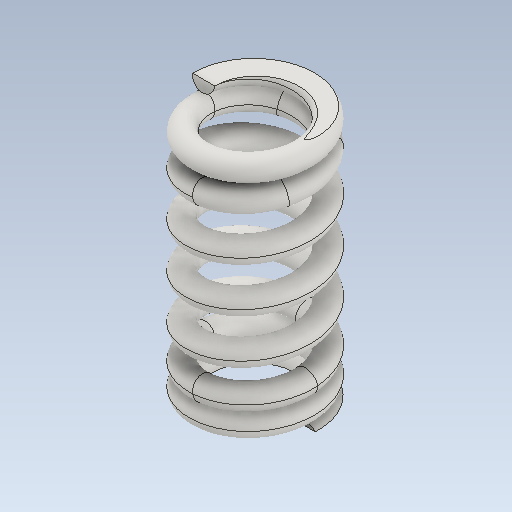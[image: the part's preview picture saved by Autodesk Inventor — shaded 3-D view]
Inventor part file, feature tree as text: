
AUTODESK INVENTOR PART (.ipt)
format: ipt  version: 2021 (Build 250183000, 183)  size: 1,066,496 bytes
history: native  units: mm
features: other x67, extrude x8, helix x5, sketch x3, sweep x2, plane x1
ambient origin geometry x8: Origin, YZ Plane, XZ Plane, XY Plane, X Axis, Y Axis, Z Axis, Center Point
bodies: Solid1 (feature_tree)
feature tree (86):
  other  "Main Coil Path(Right)"
  other  "Section Work Plane(Right)"
  other  "Start Work Plane(Right)"
  other  "End Work Plane(Right)"
  other  "End Cut Work Plane(Right)"
  other  "Start Cut Work Plane(Right)"
  other  "Plain Ends Cut Work Plane 1(Right)"
  other  "Plain Ends Cut Work Plane 2(Right)"
  sweep  "Main Coil Feature(R)"
  other  "Start Transition Coil 1(Right)"
  helix  "Coil  Start Transition 2(R)"  [1 undecoded]
  helix  "Coil  Start Transition 3(R)"  [1 undecoded]
  helix  "Coil  Start Transition 4(R)"  [1 undecoded]
  other  "Start Ends Coil(Right)"
  extrude  "Start Cut Feature(Right)"  Depth=10.0mm
  other  "End Transition Coil 1(Right)"
  other  "End Transition Coil 2(Right)"
  other  "End Transition Coil 3(Right)"
  other  "End Transition Coil 4(Right)"
  other  "End Coil(Right)"
  extrude  "End Cut Feature(Right)"  Depth=10.0mm
  extrude  "Plain Ends Cut Feature 1(Right)"  Depth=10.0mm
  extrude  "Plain Ends Cut  2(R)"  Depth=10.0mm TaperAngle=0.0deg
  other  "Main Coil Path(Left)"
  other  "Section Work Plane(Left)"
  other  "Start Work Plane(Left)"
  other  "End Work Plane(Left)"
  other  "End Cut Work Plane(Left)"
  other  "Start Cut Work Plane(Left)"
  other  "Plain Ends Cut Work Plane 1(Left)"
  other  "Plain Ends Cut Work Plane 2(Left)"
  sweep  "Main Coil Feature(L)"
  other  "Start Transition Coil 1(Left)"
  other  "Start Transition Coil 2(Left)"
  other  "Start Transition Coil 3(Left)"
  other  "Start Transition Coil 4(Left)"
  other  "Start Ends Coil(Left)"
  extrude  "Start Cut Feature(Left)"  Depth=10.0mm TaperAngle=0.0deg
  other  "End Transition Coil 1(Left)"
  other  "End Transition Coil 2(Left)"
  other  "End Transition Coil 3(Left)"
  other  "End Transition Coil 4(Left)"
  other  "End Coil(Left)"
  extrude  "End Cut Feature(Left)"  Depth=10.0mm
  extrude  "Cut Plain Ends Cut 1(L)"  TaperAngle=0.0deg  [1 undecoded]
  extrude  "Cut Plain Ends Cut 2(L)"  TaperAngle=0.0deg  [1 undecoded]
  other  "iMate Based Work Plane"
  other  "Preview Center Point"
  other  "Preview X Axis"
  other  "Path Section Sketch(Right)"
  other  "Srf1"
  helix  "Coil Section Sketch(Right)"  [1 undecoded]
  other  "Start Transition Coil Sketch 1(Right)"
  sketch  "Sketch  Start Transition 2(R)"  dims[d0=1.775mm d2=14.264373mm d3=10.0mm d4=32.5mm]
  sketch  "Sketch  Start Transition 3(R)"  dims[d5=0.0mm d6=90.0deg d7=90.0deg d8=0.0mm d9=0.0mm d12=14.440296mm d13=-18.678777mm d14=7.1mm]
  sketch  "Sketch  Start Transition 4(R)"  dims[d15=0.0mm d16=12.47328mm d17=10.0mm d18=2.5mm d19=0.0mm d20=90.0deg d21=90.0deg d22=0.0mm d23=0.0mm d24=10.682187mm d25=10.0mm d26=2.5mm d27=0.0mm d28=90.0deg d29=90.0deg d30=0.0mm d31=0.0mm d32=8.891093mm d33=10.0mm d34=2.5mm d35=0.0mm d36=90.0deg d37=90.0deg d38=0.0mm d39=0.0mm d40=7.1mm d41=10.0mm d42=2.5mm d43=0.0mm d44=90.0deg d45=90.0deg d46=0.0mm d47=0.0mm d48=12.47328mm d49=10.0mm d50=1.875mm d51=0.0mm d52=90.0deg d53=90.0deg d54=0.0mm d55=0.0mm d56=10.682187mm d57=10.0mm d58=1.875mm d59=0.0mm d60=90.0deg d61=90.0deg d62=0.0mm d63=0.0mm d64=8.891093mm d65=10.0mm d66=1.875mm d67=0.0mm d68=90.0deg d69=90.0deg d70=0.0mm d71=0.0mm d72=7.1mm d73=10.0mm d74=1.875mm d75=0.0mm d76=90.0deg d77=90.0deg d78=0.0mm d79=0.0mm d81=10.0mm d82=15.0mm d83=0.0mm d84=90.0deg d85=90.0deg d86=0.0mm d87=0.0mm d88=7.167284mm d89=10.0mm d90=10.0mm d91=0.0mm d92=90.0deg d93=90.0deg d94=0.0mm d95=0.0mm d96=40.003mm d97=7.167284mm d98=0.0mm d99=40.003mm d100=7.167284mm d101=0.0mm d102=0.0mm d103=0.0mm d104=0.0mm d105=0.0mm d106=0.0mm d108=0.0mm d112=0.0mm d113=0.0mm d114=0.0mm d121=1.858789mm d131=0.0mm d132=0.0mm d133=0.0mm d134=0.0mm d135=1.775mm d137=14.264373mm d138=10.0mm d139=32.5mm d140=0.0mm d141=90.0deg d142=90.0deg d143=0.0mm d144=0.0mm d145=14.440296mm d146=-18.678777mm d147=1.858789mm d148=0.066968mm d149=7.1mm d150=0.0mm d151=0.0mm d152=12.47328mm d153=10.0mm d154=2.5mm d155=0.0mm d156=90.0deg d157=90.0deg d158=0.0mm d159=0.0mm d160=10.682187mm d161=10.0mm d162=2.5mm d163=0.0mm d164=90.0deg d165=90.0deg d166=0.0mm d167=0.0mm d168=8.891093mm d169=10.0mm d170=2.5mm d171=0.0mm d172=90.0deg d173=90.0deg d174=0.0mm d175=0.0mm d176=7.1mm d177=10.0mm d178=2.5mm d179=0.0mm d180=90.0deg d181=90.0deg d182=0.0mm d183=0.0mm d184=10.0mm d185=10.0mm d186=10.0mm d187=10.0mm d188=7.167284mm d189=10.0mm d190=15.0mm d191=0.0mm d192=90.0deg d193=90.0deg d194=0.0mm d195=0.0mm d196=10.0mm d197=40.003mm d198=7.167284mm d199=0.0mm d200=10.0mm d201=12.47328mm d202=10.0mm d203=1.875mm d204=0.0mm d205=90.0deg d206=90.0deg d207=0.0mm d208=0.0mm d209=10.0mm d210=10.682187mm d211=10.0mm d212=1.875mm d213=0.0mm d214=90.0deg d215=90.0deg d216=0.0mm d217=0.0mm d218=8.891093mm d219=10.0mm d220=1.875mm d221=0.0mm d222=90.0deg d223=90.0deg d224=0.0mm d225=0.0mm d226=7.1mm d227=10.0mm d228=1.875mm d229=0.0mm d230=90.0deg d231=90.0deg d232=0.0mm d233=0.0mm d234=10.0mm d235=10.0mm d236=10.0mm d237=7.167284mm d238=10.0mm d239=10.0mm d240=0.0mm d241=90.0deg d242=90.0deg d243=0.0mm d244=0.0mm d245=40.003mm d246=7.167284mm d247=0.0mm d248=10.0mm d249=10.0mm d254=40.003mm d255=10.0mm d256=0.0mm d257=20.0mm d258=-0.066968mm d259=40.003mm d260=10.0mm d261=0.0mm d262=10.0mm d263=40.003mm d264=10.0mm d265=0.0mm d266=10.0mm d267=0.0mm d270=-17.791277mm d271=0.0mm d272=40.003mm d273=10.0mm d274=0.0mm d275=20.0mm d276=-157.079633mm d277=32.903mm d278=32.903mm d279=0.0mm d280=0.0mm]
  other  "End Transition Coil Sketch 1(Right)"
  other  "End Transition Coil Sketch 2(Right)"
  other  "End Transition Coil Sketch 3(Right)"
  other  "End Transition Coil Sketch 4(Right)"
  other  "Start Ends Skecth(Right)"
  other  "End Coil Skecth(Right)"
  other  "End Cut Sketch(Right)"
  other  "Start Cut Sketch(Right)"
  other  "Path Section Sketch(Left)"
  other  "Srf2"
  helix  "Coil Section Sketch(Left)"  [1 undecoded]
  other  "Start Transition Coil Sketch 1(Left)"
  other  "Start Transition Coil Sketch 2(Left)"
  other  "Start Transition Coil Sketch 3(Left)"
  other  "Start Transition Coil Sketch 4(Left)"
  other  "Start Ends Skecth(Left)"
  other  "Start Cut Sketch(Left)"
  other  "End Transition Coil Sketch 1(Left)"
  other  "End Transition Coil Sketch 2(Left)"
  other  "End Transition Coil Sketch 3(Left)"
  other  "End Transition Coil Sketch 4(Left)"
  other  "End Coil Skecth(Left)"
  other  "End Cut Sketch(Left)"
  other  "Plain Ends Cut Sketch 2(Left)"
  other  "Plain Ends Cut Sketch 2(Right)"
  other  "Plain Ends Cut Sketch 1(Right)"
  other  "Plain Ends Cut Sketch 1(Left)"
  plane  "Work Plane Start Section"
  other  "Basic Curve(Right)"
  other  "Basic Curve(Left)"
note: 7 required parameter values undecoded (feature->parameter linkage not recoverable at this tier; creation-order binding heuristic only, values carry confidence <= 0.55)
